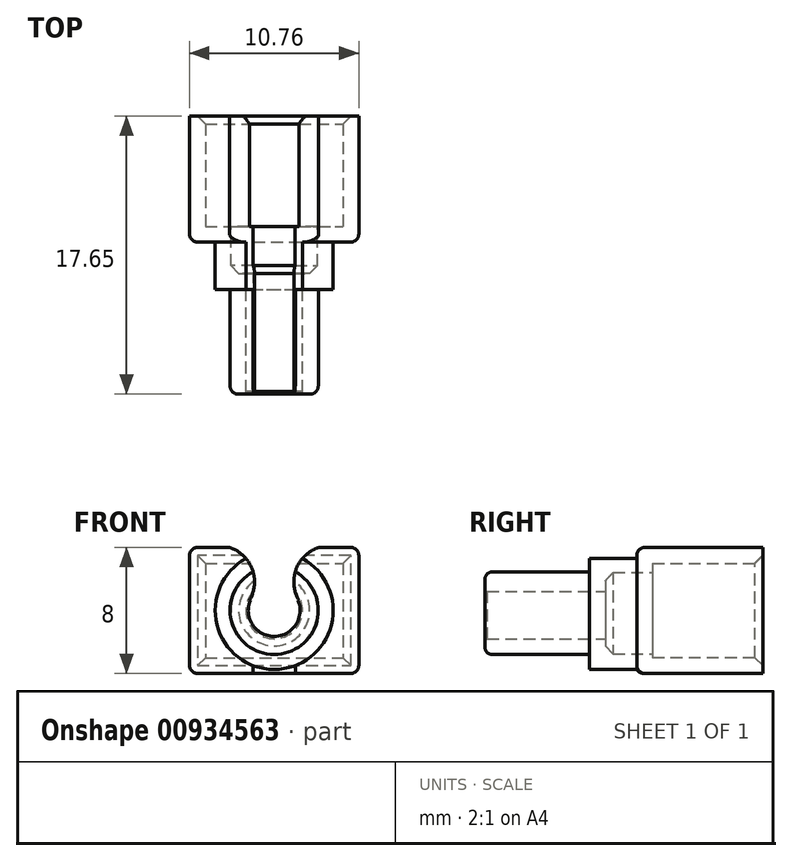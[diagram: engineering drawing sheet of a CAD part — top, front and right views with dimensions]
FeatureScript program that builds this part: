
annotation { "Feature Type Name" : "Feature", "Feature Type Description" : "" }
export const myFeature = defineFeature(function(context is Context, id is Id, definition is map)
    precondition{}
    {
        {
            var Q0;
            Q0=qCreatedBy(makeId("Front.planeOp"),FACE);
            var sketch = newSketch(context, id + "F0", { "sketchPlane" : qUnion([Q0])});
            skCircle(sketch, "E0", {"center": v(0, 0) * mm, "radius": 2.75 * mm});
            skLineSegment(sketch, "E1.bottom", {"start": v(-4.37, 3) * mm, "end": v(4.38, 3) * mm});
            skLineSegment(sketch, "E1.top", {"start": v(-4.38, -3) * mm, "end": v(4.38, -3) * mm});
            skLineSegment(sketch, "E1.left", {"start": v(-4.37, 3) * mm, "end": v(-4.38, -3) * mm});
            skLineSegment(sketch, "E1.right", {"start": v(4.38, 3) * mm, "end": v(4.38, -3) * mm});
            skSolve(sketch);
        }
        {
            var Q0;
            Q0 = qSketchRegion(id + "F0", true);
            var Q1;
            Q1=makeQuery(id+"F0.imprint","IMPRINT",FACE,{"disambiguationData":[TD([[makeQuery(id+"F0.imprint","IMPRINT",EDGE,{"derivedFrom":sQuery(id+"F0.wireOp",EDGE,"E0")}),1.0]])]});
            extrude(context, id + "F1", {"entities" : qUnion([Q0, Q1]), "oppositeDirection" : true, "depth" : 7 * mm, "offsetDistance" : 25 * mm});
        }
        {
            var Q0;
            Q0=makeQuery(id+"F1.opExtrude","CAP_FACE",FACE,{"disambiguationData":[OSD([sQuery(id+"F0.wireOp",EDGE,"E1.bottom"),sQuery(id+"F0.wireOp",EDGE,"E1.top"),sQuery(id+"F0.wireOp",EDGE,"E1.left"),sQuery(id+"F0.wireOp",EDGE,"E1.right")])],"isStart":true});
            var sketch = newSketch(context, id + "F2", { "sketchPlane" : qUnion([Q0])});
            skCircle(sketch, "E2", {"center": v(0, 0) * mm, "radius": 2.75 * mm});
            skSolve(sketch);
        }
        {
            var Q0;
            Q0 = qSketchRegion(id + "F2", true);
            extrude(context, id + "F3", {"entities" : qUnion([Q0]), "operationType" : NewBodyOperationType.ADD, "depth" : 3 * mm, "offsetDistance" : 25 * mm});
        }
        {
            var Q0;
            Q0=makeQuery(id+"F3.opExtrude","CAP_FACE",FACE,{"disambiguationData":[OSD([sQuery(id+"F2.wireOp",EDGE,"E2")])],"isStart":false});
            var sketch = newSketch(context, id + "F4", { "sketchPlane" : qUnion([Q0])});
            skCircle(sketch, "E3", {"center": v(0, 0) * mm, "radius": 1.8 * mm});
            skSolve(sketch);
        }
        {
            var Q0;
            Q0 = qSketchRegion(id + "F4", true);
            extrude(context, id + "F5", {"entities" : qUnion([Q0]), "operationType" : NewBodyOperationType.ADD, "depth" : 8 * mm, "offsetDistance" : 25 * mm});
        }
        {
            var Q0;
            Q0=makeQuery(id+"F1.opExtrude","CAP_FACE",FACE,{"disambiguationData":[OSD([sQuery(id+"F0.wireOp",EDGE,"E1.bottom"),sQuery(id+"F0.wireOp",EDGE,"E1.top"),sQuery(id+"F0.wireOp",EDGE,"E1.left"),sQuery(id+"F0.wireOp",EDGE,"E1.right")])],"isStart":false});
            shell(context, id + "F6", {"entities" : qUnion([Q0]), "thickness" : 1 * mm, "oppositeDirection" : true});
        }
        {
            var Q0;
            {var subQ0=sQuery(id+"F2.wireOp",EDGE,"E2");Q0=makeQuery(id+"F6.opShell","OFFSET_EDGE",EDGE,{"disambiguationData":[OSD([subQ0]),TDD([makeQuery(id+"F3.opExtrude","CAP_EDGE",EDGE,{"disambiguationData":[OSD([subQ0])],"isStart":true})])]});}
            var Q1;
            {var subQ0=sQuery(id+"F0.wireOp",EDGE,"E1.left");Q1=makeQuery(id+"F6.opShell","OFFSET_EDGE",EDGE,{"disambiguationData":[OSD([subQ0]),TDD([makeQuery(id+"F1.opExtrude","CAP_EDGE",EDGE,{"disambiguationData":[OSD([subQ0])],"isStart":false})])]});}
            var Q2;
            {var subQ0=sQuery(id+"F0.wireOp",EDGE,"E1.bottom");Q2=makeQuery(id+"F6.opShell","OFFSET_EDGE",EDGE,{"disambiguationData":[OSD([subQ0]),TDD([makeQuery(id+"F1.opExtrude","CAP_EDGE",EDGE,{"disambiguationData":[OSD([subQ0])],"isStart":false})])]});}
            var Q3;
            {var subQ0=sQuery(id+"F0.wireOp",EDGE,"E1.top");Q3=makeQuery(id+"F6.opShell","OFFSET_EDGE",EDGE,{"disambiguationData":[OSD([subQ0]),TDD([makeQuery(id+"F1.opExtrude","CAP_EDGE",EDGE,{"disambiguationData":[OSD([subQ0])],"isStart":false})])]});}
            var Q4;
            {var subQ0=sQuery(id+"F0.wireOp",EDGE,"E1.right");Q4=makeQuery(id+"F6.opShell","OFFSET_EDGE",EDGE,{"disambiguationData":[OSD([subQ0]),TDD([makeQuery(id+"F1.opExtrude","CAP_EDGE",EDGE,{"disambiguationData":[OSD([subQ0])],"isStart":false})])]});}
            var Q5;
            {var subQ0=sQuery(id+"F4.wireOp",EDGE,"E3");Q5=makeQuery(id+"F6.opShell","OFFSET_EDGE",EDGE,{"disambiguationData":[OSD([subQ0]),TDD([makeQuery(id+"F5.opExtrude","CAP_EDGE",EDGE,{"disambiguationData":[OSD([subQ0])],"isStart":true})])]});}
            chamfer(context, id + "F7", {"entities" : qUnion([Q0, Q1, Q2, Q3, Q4, Q5]), "width" : .5 * mm, "tangentPropagation" : true});
        }
        {
            var Q0;
            Q0=makeQuery(id+"F1.opExtrude","SWEPT_FACE",FACE,{"disambiguationData":[OSD([sQuery(id+"F0.wireOp",EDGE,"E1.bottom")])]});
            var sketch = newSketch(context, id + "F8", { "sketchPlane" : qUnion([Q0])});
            skLineSegment(sketch, "E4", {"start": v(-3.71, -10.65) * mm, "end": v(4.47, -10.65) * mm});
            skLineSegment(sketch, "E5", {"start": v(4.47, -10.65) * mm, "end": v(0, -20.75) * mm});
            skLineSegment(sketch, "E6", {"start": v(0, -20.75) * mm, "end": v(-3.71, -10.65) * mm});
            skSolve(sketch);
        }
        {
            var Q0;
            Q0 = qSketchRegion(id + "F8", true);
            extrude(context, id + "F9", {"entities" : qUnion([Q0]), "operationType" : NewBodyOperationType.REMOVE, "oppositeDirection" : true, "depth" : 25 * mm, "offsetDistance" : 25 * mm});
        }
        {
            var Q0;
            Q0=makeQuery(id+"F7.opChamfer","SPLIT",FACE,{"disambiguationData":[OD(1.0)],"derivedFrom":makeQuery(id+"F6.opShell","OFFSET_FACE",FACE,{"disambiguationData":[OSD([sQuery(id+"F0.wireOp",EDGE,"E1.bottom"),sQuery(id+"F0.wireOp",EDGE,"E1.top"),sQuery(id+"F0.wireOp",EDGE,"E1.left"),sQuery(id+"F0.wireOp",EDGE,"E1.right")])]})});
            var sketch = newSketch(context, id + "F10", { "sketchPlane" : qUnion([Q0])});
            skArc(sketch, "E7", {"start": v(-1.57, 0.65) * mm, "mid": v(-1.53, 2.93) * mm, "end": v(-3.48, 4.11) * mm});
            skArc(sketch, "E8.MirrorC", {"start": v(1.57, 0.65) * mm, "mid": v(1.53, 2.93) * mm, "end": v(3.48, 4.11) * mm});
            skLineSegment(sketch, "E9", {"start": v(-3.48, 4.11) * mm, "end": v(3.48, 4.11) * mm});
            skLineSegment(sketch, "E10", {"start": v(-1.57, 0.65) * mm, "end": v(1.57, 0.65) * mm});
            skPoint(sketch, "E11.start.orphan", {"position": v(-2.13, 0) * mm});
            skSolve(sketch);
        }
        {
            var Q0;
            Q0 = qSketchRegion(id + "F10", true);
            extrude(context, id + "F11", {"entities" : qUnion([Q0]), "operationType" : NewBodyOperationType.REMOVE, "endBound" : BoundingType.SYMMETRIC, "oppositeDirection" : true, "depth" : 46 * mm, "offsetDistance" : 25 * mm});
        }
        {
            var Q0;
            Q0=makeQuery(id+"F1.opExtrude","SWEPT_EDGE",EDGE,{"disambiguationData":[OSD([sQuery(id+"F0.wireOp",EDGE,"E1.bottom"),sQuery(id+"F0.wireOp",EDGE,"E1.right")])]});
            var Q1;
            Q1=makeQuery(id+"F1.opExtrude","SWEPT_EDGE",EDGE,{"disambiguationData":[OSD([sQuery(id+"F0.wireOp",EDGE,"E1.top"),sQuery(id+"F0.wireOp",EDGE,"E1.right")])]});
            var Q2;
            Q2=makeQuery(id+"F1.opExtrude","SWEPT_EDGE",EDGE,{"disambiguationData":[OSD([sQuery(id+"F0.wireOp",EDGE,"E1.bottom"),sQuery(id+"F0.wireOp",EDGE,"E1.left")])]});
            var Q3;
            Q3=makeQuery(id+"F1.opExtrude","SWEPT_EDGE",EDGE,{"disambiguationData":[OSD([sQuery(id+"F0.wireOp",EDGE,"E1.top"),sQuery(id+"F0.wireOp",EDGE,"E1.left")])]});
            var Q4;
            Q4=makeQuery(id+"F1.opExtrude","CAP_EDGE",EDGE,{"disambiguationData":[OSD([sQuery(id+"F0.wireOp",EDGE,"E1.left")])],"isStart":true});
            var Q5;
            {var subQ0=sQuery(id+"F0.wireOp",EDGE,"E1.bottom");var subQ1=sQuery(id+"F0.wireOp",EDGE,"E1.left");Q5=makeQuery(id+"F11.boolean.opBoolean","SPLIT",EDGE,{"disambiguationData":[TD([makeQuery(id+"F1.opExtrude","SWEPT_FACE",FACE,{"disambiguationData":[OSD([subQ1])]})])],"derivedFrom":makeQuery(id+"F1.opExtrude","CAP_EDGE",EDGE,{"disambiguationData":[OSD([subQ0])],"isStart":true})});}
            var Q6;
            {var subQ0=sQuery(id+"F0.wireOp",EDGE,"E1.bottom");var subQ1=sQuery(id+"F0.wireOp",EDGE,"E1.right");Q6=makeQuery(id+"F11.boolean.opBoolean","SPLIT",EDGE,{"disambiguationData":[TD([makeQuery(id+"F1.opExtrude","SWEPT_FACE",FACE,{"disambiguationData":[OSD([subQ1])]})])],"derivedFrom":makeQuery(id+"F1.opExtrude","CAP_EDGE",EDGE,{"disambiguationData":[OSD([subQ0])],"isStart":true})});}
            var Q7;
            Q7=makeQuery(id+"F1.opExtrude","CAP_EDGE",EDGE,{"disambiguationData":[OSD([sQuery(id+"F0.wireOp",EDGE,"E1.right")])],"isStart":true});
            var Q8;
            Q8=makeQuery(id+"F1.opExtrude","CAP_EDGE",EDGE,{"disambiguationData":[OSD([sQuery(id+"F0.wireOp",EDGE,"E1.top")])],"isStart":true});
            var Q9;
            Q9=makeQuery(id+"F9.boolean.opBoolean","INTERSECT",EDGE,{"derivedFrom":[makeQuery(id+"F5.opExtrude","SWEPT_FACE",FACE,{"disambiguationData":[OSD([sQuery(id+"F4.wireOp",EDGE,"E3")])]}),makeQuery(id+"F9.opExtrude","SWEPT_FACE",FACE,{"disambiguationData":[OSD([sQuery(id+"F8.wireOp",EDGE,"E4")])]})]});
            fillet(context, id + "F12", {"entities" : qUnion([Q0, Q1, Q2, Q3, Q4, Q5, Q6, Q7, Q8, Q9]), "radius" : .5 * mm, "tangentPropagation" : true, "allowEdgeOverflow" : false});
        }
    });
